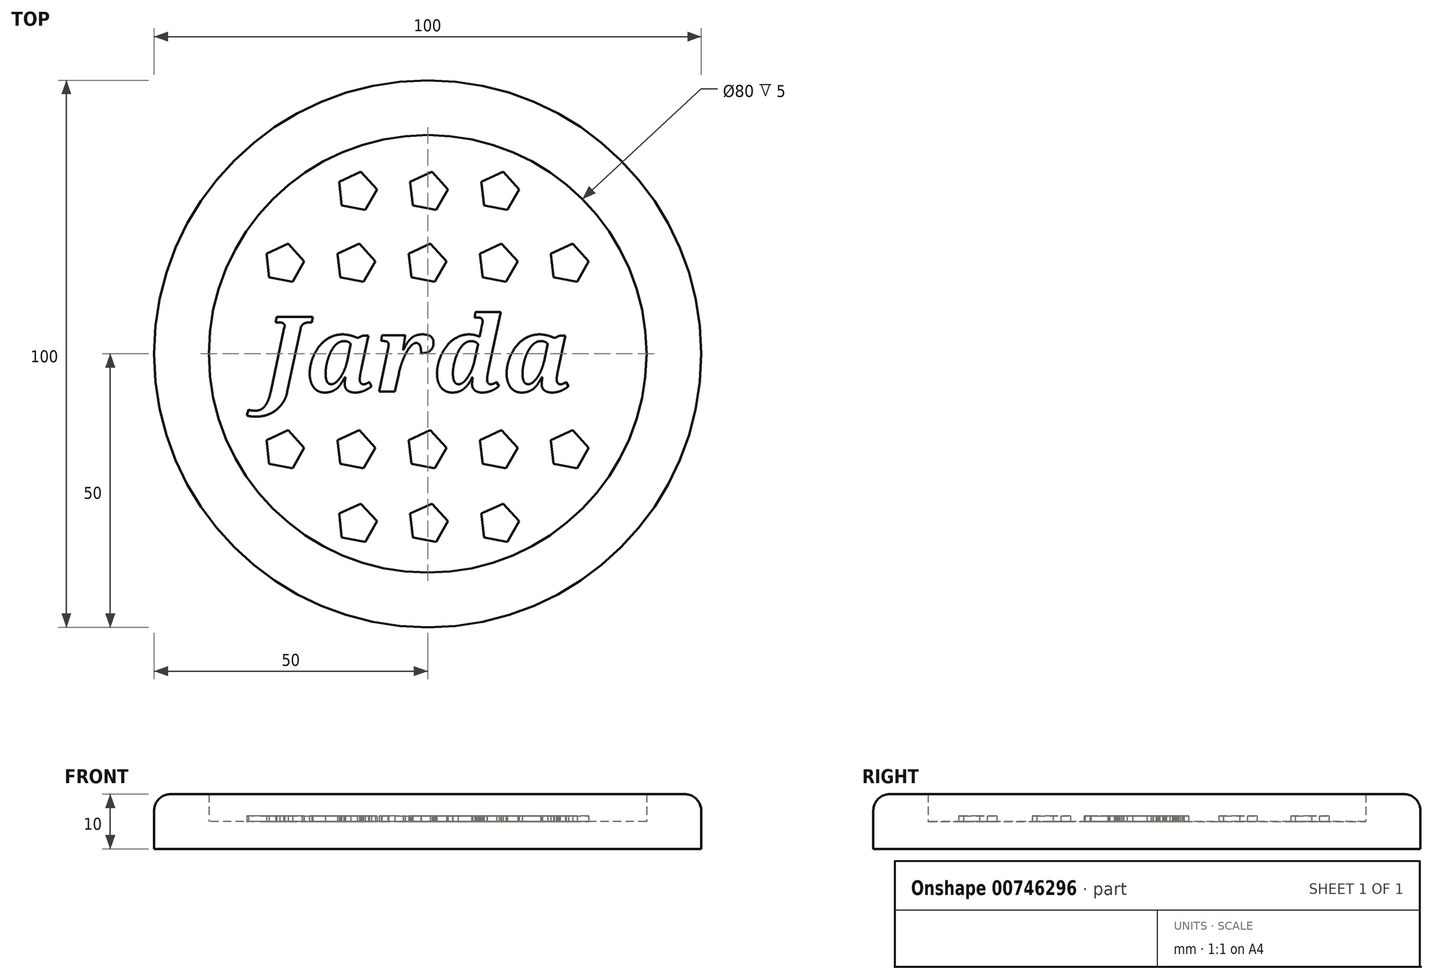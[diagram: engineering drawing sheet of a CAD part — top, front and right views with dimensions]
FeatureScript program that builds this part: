
annotation { "Feature Type Name" : "Feature", "Feature Type Description" : "" }
export const myFeature = defineFeature(function(context is Context, id is Id, definition is map)
    precondition{}
    {
        {
            var Q0;
            Q0=qCreatedBy(makeId("Top.planeOp"),FACE);
            var sketch = newSketch(context, id + "F0", { "sketchPlane" : qUnion([Q0])});
            skCircle(sketch, "E0", {"center": v(0, 0) * mm, "radius": 50 * mm});
            skCircle(sketch, "E1", {"center": v(0, 0) * mm, "radius": 40 * mm});
            skText(sketch, "E2", { "text": "Jarda", "fontName": "NotoSerif-BoldItalic.ttf"});
            skCircle(sketch, "E3.cCircle", {"center": v(-26.24, 16.51) * mm, "radius": 3 * mm, "construction": true});
            skLineSegment(sketch, "E3.0", {"start": v(-22.55, 16.94) * mm, "end": v(-24.7, 13.14) * mm});
            skLineSegment(sketch, "E3.1", {"start": v(-24.7, 13.14) * mm, "end": v(-28.97, 14) * mm});
            skLineSegment(sketch, "E3.2", {"start": v(-28.97, 14) * mm, "end": v(-29.47, 18.34) * mm});
            skLineSegment(sketch, "E3.3", {"start": v(-29.47, 18.34) * mm, "end": v(-25.5, 20.15) * mm});
            skLineSegment(sketch, "E3.4", {"start": v(-25.5, 20.15) * mm, "end": v(-22.55, 16.94) * mm});
            skPoint(sketch, "E3.0.midPoint", {"position": v(-23.62, 15.04) * mm});
            skPoint(sketch, "E4.0.1.0", {"position": v(-23.62, -19.06) * mm});
            skLineSegment(sketch, "E4.0.1.1", {"start": v(-25.5, -13.95) * mm, "end": v(-22.55, -17.16) * mm});
            skLineSegment(sketch, "E4.0.1.2", {"start": v(-29.47, -15.76) * mm, "end": v(-25.5, -13.95) * mm});
            skLineSegment(sketch, "E4.0.1.3", {"start": v(-28.97, -20.1) * mm, "end": v(-29.47, -15.76) * mm});
            skLineSegment(sketch, "E4.0.1.4", {"start": v(-24.7, -20.96) * mm, "end": v(-28.97, -20.1) * mm});
            skCircle(sketch, "E4.0.1.5", {"center": v(-26.24, -17.59) * mm, "radius": 3 * mm, "construction": true});
            skLineSegment(sketch, "E4.0.1.6", {"start": v(-22.55, -17.16) * mm, "end": v(-24.7, -20.96) * mm});
            skPoint(sketch, "E4.1.0.0", {"position": v(-10.62, 15.04) * mm});
            skLineSegment(sketch, "E4.1.0.1", {"start": v(-12.5, 20.15) * mm, "end": v(-9.55, 16.94) * mm});
            skLineSegment(sketch, "E4.1.0.2", {"start": v(-16.47, 18.34) * mm, "end": v(-12.5, 20.15) * mm});
            skLineSegment(sketch, "E4.1.0.3", {"start": v(-15.97, 14) * mm, "end": v(-16.47, 18.34) * mm});
            skLineSegment(sketch, "E4.1.0.4", {"start": v(-11.7, 13.14) * mm, "end": v(-15.97, 14) * mm});
            skCircle(sketch, "E4.1.0.5", {"center": v(-13.24, 16.51) * mm, "radius": 3 * mm, "construction": true});
            skLineSegment(sketch, "E4.1.0.6", {"start": v(-9.55, 16.94) * mm, "end": v(-11.7, 13.14) * mm});
            skPoint(sketch, "E4.1.1.0", {"position": v(-10.62, -19.06) * mm});
            skLineSegment(sketch, "E4.1.1.1", {"start": v(-12.5, -13.95) * mm, "end": v(-9.55, -17.16) * mm});
            skLineSegment(sketch, "E4.1.1.2", {"start": v(-16.47, -15.76) * mm, "end": v(-12.5, -13.95) * mm});
            skLineSegment(sketch, "E4.1.1.3", {"start": v(-15.97, -20.1) * mm, "end": v(-16.47, -15.76) * mm});
            skLineSegment(sketch, "E4.1.1.4", {"start": v(-11.7, -20.96) * mm, "end": v(-15.97, -20.1) * mm});
            skCircle(sketch, "E4.1.1.5", {"center": v(-13.24, -17.59) * mm, "radius": 3 * mm, "construction": true});
            skLineSegment(sketch, "E4.1.1.6", {"start": v(-9.55, -17.16) * mm, "end": v(-11.7, -20.96) * mm});
            skPoint(sketch, "E4.2.0.0", {"position": v(2.38, 15.04) * mm});
            skLineSegment(sketch, "E4.2.0.1", {"start": v(0.5, 20.15) * mm, "end": v(3.45, 16.94) * mm});
            skLineSegment(sketch, "E4.2.0.2", {"start": v(-3.47, 18.34) * mm, "end": v(0.5, 20.15) * mm});
            skLineSegment(sketch, "E4.2.0.3", {"start": v(-2.97, 14) * mm, "end": v(-3.47, 18.34) * mm});
            skLineSegment(sketch, "E4.2.0.4", {"start": v(1.3, 13.14) * mm, "end": v(-2.97, 14) * mm});
            skCircle(sketch, "E4.2.0.5", {"center": v(-0.24, 16.51) * mm, "radius": 3 * mm, "construction": true});
            skLineSegment(sketch, "E4.2.0.6", {"start": v(3.45, 16.94) * mm, "end": v(1.3, 13.14) * mm});
            skPoint(sketch, "E4.2.1.0", {"position": v(2.38, -19.06) * mm});
            skLineSegment(sketch, "E4.2.1.1", {"start": v(0.5, -13.95) * mm, "end": v(3.45, -17.16) * mm});
            skLineSegment(sketch, "E4.2.1.2", {"start": v(-3.47, -15.76) * mm, "end": v(0.5, -13.95) * mm});
            skLineSegment(sketch, "E4.2.1.3", {"start": v(-2.97, -20.1) * mm, "end": v(-3.47, -15.76) * mm});
            skLineSegment(sketch, "E4.2.1.4", {"start": v(1.3, -20.96) * mm, "end": v(-2.97, -20.1) * mm});
            skCircle(sketch, "E4.2.1.5", {"center": v(-0.24, -17.59) * mm, "radius": 3 * mm, "construction": true});
            skLineSegment(sketch, "E4.2.1.6", {"start": v(3.45, -17.16) * mm, "end": v(1.3, -20.96) * mm});
            skPoint(sketch, "E4.3.0.0", {"position": v(15.38, 15.04) * mm});
            skLineSegment(sketch, "E4.3.0.1", {"start": v(13.5, 20.15) * mm, "end": v(16.45, 16.94) * mm});
            skLineSegment(sketch, "E4.3.0.2", {"start": v(9.53, 18.34) * mm, "end": v(13.5, 20.15) * mm});
            skLineSegment(sketch, "E4.3.0.3", {"start": v(10.03, 14) * mm, "end": v(9.53, 18.34) * mm});
            skLineSegment(sketch, "E4.3.0.4", {"start": v(14.3, 13.14) * mm, "end": v(10.03, 14) * mm});
            skCircle(sketch, "E4.3.0.5", {"center": v(12.76, 16.51) * mm, "radius": 3 * mm, "construction": true});
            skLineSegment(sketch, "E4.3.0.6", {"start": v(16.45, 16.94) * mm, "end": v(14.3, 13.14) * mm});
            skPoint(sketch, "E4.3.1.0", {"position": v(15.38, -19.06) * mm});
            skLineSegment(sketch, "E4.3.1.1", {"start": v(13.5, -13.95) * mm, "end": v(16.45, -17.16) * mm});
            skLineSegment(sketch, "E4.3.1.2", {"start": v(9.53, -15.76) * mm, "end": v(13.5, -13.95) * mm});
            skLineSegment(sketch, "E4.3.1.3", {"start": v(10.03, -20.1) * mm, "end": v(9.53, -15.76) * mm});
            skLineSegment(sketch, "E4.3.1.4", {"start": v(14.3, -20.96) * mm, "end": v(10.03, -20.1) * mm});
            skCircle(sketch, "E4.3.1.5", {"center": v(12.76, -17.59) * mm, "radius": 3 * mm, "construction": true});
            skLineSegment(sketch, "E4.3.1.6", {"start": v(16.45, -17.16) * mm, "end": v(14.3, -20.96) * mm});
            skPoint(sketch, "E4.4.0.0", {"position": v(28.38, 15.04) * mm});
            skLineSegment(sketch, "E4.4.0.1", {"start": v(26.5, 20.15) * mm, "end": v(29.45, 16.94) * mm});
            skLineSegment(sketch, "E4.4.0.2", {"start": v(22.53, 18.34) * mm, "end": v(26.5, 20.15) * mm});
            skLineSegment(sketch, "E4.4.0.3", {"start": v(23.03, 14) * mm, "end": v(22.53, 18.34) * mm});
            skLineSegment(sketch, "E4.4.0.4", {"start": v(27.3, 13.14) * mm, "end": v(23.03, 14) * mm});
            skCircle(sketch, "E4.4.0.5", {"center": v(25.76, 16.51) * mm, "radius": 3 * mm, "construction": true});
            skLineSegment(sketch, "E4.4.0.6", {"start": v(29.45, 16.94) * mm, "end": v(27.3, 13.14) * mm});
            skPoint(sketch, "E4.4.1.0", {"position": v(28.38, -19.06) * mm});
            skLineSegment(sketch, "E4.4.1.1", {"start": v(26.5, -13.95) * mm, "end": v(29.45, -17.16) * mm});
            skLineSegment(sketch, "E4.4.1.2", {"start": v(22.53, -15.76) * mm, "end": v(26.5, -13.95) * mm});
            skLineSegment(sketch, "E4.4.1.3", {"start": v(23.03, -20.1) * mm, "end": v(22.53, -15.76) * mm});
            skLineSegment(sketch, "E4.4.1.4", {"start": v(27.3, -20.96) * mm, "end": v(23.03, -20.1) * mm});
            skCircle(sketch, "E4.4.1.5", {"center": v(25.76, -17.59) * mm, "radius": 3 * mm, "construction": true});
            skLineSegment(sketch, "E4.4.1.6", {"start": v(29.45, -17.16) * mm, "end": v(27.3, -20.96) * mm});
            skLineSegment(sketch, "E4.direction1", {"start": v(-28.97, 14) * mm, "end": v(-15.97, 14) * mm, "construction": true});
            skLineSegment(sketch, "E4.direction2", {"start": v(-28.97, 14) * mm, "end": v(-28.97, -20.1) * mm, "construction": true});
            skPoint(sketch, "E5.2.1.0", {"position": v(-10.35, -32.51) * mm});
            skLineSegment(sketch, "E5.2.1.1", {"start": v(-12.23, -27.4) * mm, "end": v(-9.28, -30.61) * mm});
            skLineSegment(sketch, "E5.2.1.2", {"start": v(-16.2, -29.21) * mm, "end": v(-12.23, -27.4) * mm});
            skLineSegment(sketch, "E5.2.1.3", {"start": v(-15.7, -33.54) * mm, "end": v(-16.2, -29.21) * mm});
            skLineSegment(sketch, "E5.2.1.4", {"start": v(-11.42, -34.4) * mm, "end": v(-15.7, -33.54) * mm});
            skCircle(sketch, "E5.2.1.5", {"center": v(-12.96, -31.04) * mm, "radius": 3 * mm, "construction": true});
            skLineSegment(sketch, "E5.2.1.6", {"start": v(-9.28, -30.61) * mm, "end": v(-11.42, -34.4) * mm});
            skLineSegment(sketch, "E6.1.0.0", {"start": v(1.58, -34.4) * mm, "end": v(-2.7, -33.54) * mm});
            skLineSegment(sketch, "E6.1.0.1", {"start": v(-3.2, -29.21) * mm, "end": v(0.77, -27.4) * mm});
            skLineSegment(sketch, "E6.1.0.2", {"start": v(0.77, -27.4) * mm, "end": v(3.72, -30.61) * mm});
            skPoint(sketch, "E6.1.0.3", {"position": v(2.65, -32.51) * mm});
            skLineSegment(sketch, "E6.1.0.4", {"start": v(-2.7, -33.54) * mm, "end": v(-3.2, -29.21) * mm});
            skLineSegment(sketch, "E6.1.0.5", {"start": v(3.72, -30.61) * mm, "end": v(1.58, -34.4) * mm});
            skCircle(sketch, "E6.1.0.6", {"center": v(0.04, -31.04) * mm, "radius": 3 * mm, "construction": true});
            skLineSegment(sketch, "E6.2.0.0", {"start": v(14.58, -34.4) * mm, "end": v(10.3, -33.54) * mm});
            skLineSegment(sketch, "E6.2.0.1", {"start": v(9.8, -29.21) * mm, "end": v(13.77, -27.4) * mm});
            skLineSegment(sketch, "E6.2.0.2", {"start": v(13.77, -27.4) * mm, "end": v(16.72, -30.61) * mm});
            skPoint(sketch, "E6.2.0.3", {"position": v(15.65, -32.51) * mm});
            skLineSegment(sketch, "E6.2.0.4", {"start": v(10.3, -33.54) * mm, "end": v(9.8, -29.21) * mm});
            skLineSegment(sketch, "E6.2.0.5", {"start": v(16.72, -30.61) * mm, "end": v(14.58, -34.4) * mm});
            skCircle(sketch, "E6.2.0.6", {"center": v(13.04, -31.04) * mm, "radius": 3 * mm, "construction": true});
            skLineSegment(sketch, "E6.direction1", {"start": v(-15.7, -33.54) * mm, "end": v(-2.7, -33.54) * mm, "construction": true});
            skLineSegment(sketch, "E7.0.1.0", {"start": v(1.58, 26.3) * mm, "end": v(-2.7, 27.16) * mm});
            skLineSegment(sketch, "E7.0.1.1", {"start": v(0.77, 33.3) * mm, "end": v(3.72, 30.09) * mm});
            skLineSegment(sketch, "E7.0.1.2", {"start": v(-15.7, 27.16) * mm, "end": v(-2.7, 27.16) * mm, "construction": true});
            skLineSegment(sketch, "E7.0.1.3", {"start": v(-12.23, 33.3) * mm, "end": v(-9.28, 30.09) * mm});
            skPoint(sketch, "E7.0.1.4", {"position": v(-10.35, 28.19) * mm});
            skLineSegment(sketch, "E7.0.1.5", {"start": v(-2.7, 27.16) * mm, "end": v(-3.2, 31.49) * mm});
            skCircle(sketch, "E7.0.1.6", {"center": v(-12.96, 29.66) * mm, "radius": 3 * mm, "construction": true});
            skPoint(sketch, "E7.0.1.7", {"position": v(2.65, 28.19) * mm});
            skCircle(sketch, "E7.0.1.8", {"center": v(0.04, 29.66) * mm, "radius": 3 * mm, "construction": true});
            skLineSegment(sketch, "E7.0.1.9", {"start": v(14.58, 26.3) * mm, "end": v(10.3, 27.16) * mm});
            skPoint(sketch, "E7.0.1.10", {"position": v(15.65, 28.19) * mm});
            skCircle(sketch, "E7.0.1.11", {"center": v(13.04, 29.66) * mm, "radius": 3 * mm, "construction": true});
            skLineSegment(sketch, "E7.0.1.12", {"start": v(-9.28, 30.09) * mm, "end": v(-11.42, 26.3) * mm});
            skLineSegment(sketch, "E7.0.1.13", {"start": v(-3.2, 31.49) * mm, "end": v(0.77, 33.3) * mm});
            skLineSegment(sketch, "E7.0.1.14", {"start": v(-15.7, 27.16) * mm, "end": v(-16.2, 31.49) * mm});
            skLineSegment(sketch, "E7.0.1.15", {"start": v(-11.42, 26.3) * mm, "end": v(-15.7, 27.16) * mm});
            skLineSegment(sketch, "E7.0.1.16", {"start": v(3.72, 30.09) * mm, "end": v(1.58, 26.3) * mm});
            skLineSegment(sketch, "E7.0.1.17", {"start": v(16.72, 30.09) * mm, "end": v(14.58, 26.3) * mm});
            skLineSegment(sketch, "E7.0.1.18", {"start": v(9.8, 31.49) * mm, "end": v(13.77, 33.3) * mm});
            skLineSegment(sketch, "E7.0.1.19", {"start": v(13.77, 33.3) * mm, "end": v(16.72, 30.09) * mm});
            skLineSegment(sketch, "E7.0.1.20", {"start": v(10.3, 27.16) * mm, "end": v(9.8, 31.49) * mm});
            skLineSegment(sketch, "E7.0.1.21", {"start": v(-16.2, 31.49) * mm, "end": v(-12.23, 33.3) * mm});
            skLineSegment(sketch, "E7.direction1", {"start": v(-15.7, -33.54) * mm, "end": v(9.3, -33.54) * mm, "construction": true});
            skLineSegment(sketch, "E7.direction2", {"start": v(-15.7, -33.54) * mm, "end": v(-15.7, 27.16) * mm, "construction": true});
            const initialGuessF0  = {"E2": [-0.03, -0.00689, 1, 0, 0.01378]};
            skSetInitialGuess(sketch, initialGuessF0);
            skSolve(sketch);
        }
        {
            var Q0;
            Q0=makeQuery(id+"F0.imprint","IMPRINT",FACE,{"disambiguationData":[TD([[makeQuery(id+"F0.imprint","IMPRINT",EDGE,{"derivedFrom":sQuery(id+"F0.wireOp",EDGE,"E0")}),1.0]])]});
            extrude(context, id + "F1", {"entities" : qUnion([Q0]), "depth" : 10 * mm, "offsetDistance" : 25 * mm});
        }
        {
            var Q0;
            Q0=makeQuery(id+"F0.imprint","IMPRINT",FACE,{"disambiguationData":[TD([[makeQuery(id+"F0.imprint","IMPRINT",EDGE,{"derivedFrom":sQuery(id+"F0.wireOp",EDGE,"E3.0")}),-1.0]])]});
            var Q1;
            Q1=makeQuery(id+"F0.imprint","IMPRINT",FACE,{"disambiguationData":[TD([[makeQuery(id+"F0.imprint","IMPRINT",EDGE,{"derivedFrom":sQuery(id+"F0.wireOp",EDGE,"E4.1.0.1")}),-1.0]])]});
            var Q2;
            Q2=makeQuery(id+"F0.imprint","IMPRINT",FACE,{"disambiguationData":[TD([[makeQuery(id+"F0.imprint","IMPRINT",EDGE,{"derivedFrom":sQuery(id+"F0.wireOp",EDGE,"E7.0.1.3")}),-1.0]])]});
            var Q3;
            Q3=makeQuery(id+"F0.imprint","IMPRINT",FACE,{"disambiguationData":[TD([[makeQuery(id+"F0.imprint","IMPRINT",EDGE,{"derivedFrom":sQuery(id+"F0.wireOp",EDGE,"E7.0.1.0")}),-1.0]])]});
            var Q4;
            Q4=makeQuery(id+"F0.imprint","IMPRINT",FACE,{"disambiguationData":[TD([[makeQuery(id+"F0.imprint","IMPRINT",EDGE,{"derivedFrom":sQuery(id+"F0.wireOp",EDGE,"E4.2.0.1")}),-1.0]])]});
            var Q5;
            Q5=makeQuery(id+"F0.imprint","IMPRINT",FACE,{"disambiguationData":[TD([[makeQuery(id+"F0.imprint","IMPRINT",EDGE,{"derivedFrom":sQuery(id+"F0.wireOp",EDGE,"E7.0.1.9")}),-1.0]])]});
            var Q6;
            Q6=makeQuery(id+"F0.imprint","IMPRINT",FACE,{"disambiguationData":[TD([[makeQuery(id+"F0.imprint","IMPRINT",EDGE,{"derivedFrom":sQuery(id+"F0.wireOp",EDGE,"E4.3.0.1")}),-1.0]])]});
            var Q7;
            Q7=makeQuery(id+"F0.imprint","IMPRINT",FACE,{"disambiguationData":[TD([[makeQuery(id+"F0.imprint","IMPRINT",EDGE,{"derivedFrom":sQuery(id+"F0.wireOp",EDGE,"E4.4.0.1")}),-1.0]])]});
            var Q8;
            Q8=makeQuery(id+"F0.imprint","IMPRINT",FACE,{"disambiguationData":[TD([[makeQuery(id+"F0.imprint","IMPRINT",EDGE,{"derivedFrom":sQuery(id+"F0.wireOp",EDGE,"E2.sketch_text.stroke-0")}),-1.0]])]});
            var Q9;
            Q9=makeQuery(id+"F0.imprint","IMPRINT",FACE,{"disambiguationData":[TD([[makeQuery(id+"F0.imprint","IMPRINT",EDGE,{"derivedFrom":sQuery(id+"F0.wireOp",EDGE,"E2.sketch_text.stroke-32")}),-1.0]])]});
            var Q10;
            Q10=makeQuery(id+"F0.imprint","IMPRINT",FACE,{"disambiguationData":[TD([[makeQuery(id+"F0.imprint","IMPRINT",EDGE,{"derivedFrom":sQuery(id+"F0.wireOp",EDGE,"E2.sketch_text.stroke-88")}),-1.0]])]});
            var Q11;
            Q11=makeQuery(id+"F0.imprint","IMPRINT",FACE,{"disambiguationData":[TD([[makeQuery(id+"F0.imprint","IMPRINT",EDGE,{"derivedFrom":sQuery(id+"F0.wireOp",EDGE,"E2.sketch_text.stroke-118")}),-1.0]])]});
            var Q12;
            Q12=makeQuery(id+"F0.imprint","IMPRINT",FACE,{"disambiguationData":[TD([[makeQuery(id+"F0.imprint","IMPRINT",EDGE,{"derivedFrom":sQuery(id+"F0.wireOp",EDGE,"E2.sketch_text.stroke-190")}),-1.0]])]});
            var Q13;
            Q13=makeQuery(id+"F0.imprint","IMPRINT",FACE,{"disambiguationData":[TD([[makeQuery(id+"F0.imprint","IMPRINT",EDGE,{"derivedFrom":sQuery(id+"F0.wireOp",EDGE,"E4.0.1.1")}),-1.0]])]});
            var Q14;
            Q14=makeQuery(id+"F0.imprint","IMPRINT",FACE,{"disambiguationData":[TD([[makeQuery(id+"F0.imprint","IMPRINT",EDGE,{"derivedFrom":sQuery(id+"F0.wireOp",EDGE,"E4.1.1.1")}),-1.0]])]});
            var Q15;
            Q15=makeQuery(id+"F0.imprint","IMPRINT",FACE,{"disambiguationData":[TD([[makeQuery(id+"F0.imprint","IMPRINT",EDGE,{"derivedFrom":sQuery(id+"F0.wireOp",EDGE,"E4.2.1.1")}),-1.0]])]});
            var Q16;
            Q16=makeQuery(id+"F0.imprint","IMPRINT",FACE,{"disambiguationData":[TD([[makeQuery(id+"F0.imprint","IMPRINT",EDGE,{"derivedFrom":sQuery(id+"F0.wireOp",EDGE,"E4.3.1.1")}),-1.0]])]});
            var Q17;
            Q17=makeQuery(id+"F0.imprint","IMPRINT",FACE,{"disambiguationData":[TD([[makeQuery(id+"F0.imprint","IMPRINT",EDGE,{"derivedFrom":sQuery(id+"F0.wireOp",EDGE,"E4.4.1.1")}),-1.0]])]});
            var Q18;
            Q18=makeQuery(id+"F0.imprint","IMPRINT",FACE,{"disambiguationData":[TD([[makeQuery(id+"F0.imprint","IMPRINT",EDGE,{"derivedFrom":sQuery(id+"F0.wireOp",EDGE,"E6.2.0.0")}),-1.0]])]});
            var Q19;
            Q19=makeQuery(id+"F0.imprint","IMPRINT",FACE,{"disambiguationData":[TD([[makeQuery(id+"F0.imprint","IMPRINT",EDGE,{"derivedFrom":sQuery(id+"F0.wireOp",EDGE,"E6.1.0.0")}),-1.0]])]});
            var Q20;
            Q20=makeQuery(id+"F0.imprint","IMPRINT",FACE,{"disambiguationData":[TD([[makeQuery(id+"F0.imprint","IMPRINT",EDGE,{"derivedFrom":sQuery(id+"F0.wireOp",EDGE,"E5.2.1.1")}),-1.0]])]});
            extrude(context, id + "F2", {"entities" : qUnion([Q0, Q1, Q2, Q3, Q4, Q5, Q6, Q7, Q8, Q9, Q10, Q11, Q12, Q13, Q14, Q15, Q16, Q17, Q18, Q19, Q20]), "operationType" : NewBodyOperationType.ADD, "depth" : 6 * mm, "offsetDistance" : 25 * mm});
        }
        {
            var Q0;
            Q0=makeQuery(id+"F0.imprint","IMPRINT",FACE,{"disambiguationData":[TD([[makeQuery(id+"F0.imprint","IMPRINT",EDGE,{"derivedFrom":sQuery(id+"F0.wireOp",EDGE,"E1")}),1.0]])]});
            var Q1;
            Q1=makeQuery(id+"F0.imprint","IMPRINT",FACE,{"disambiguationData":[TD([[makeQuery(id+"F0.imprint","IMPRINT",EDGE,{"derivedFrom":sQuery(id+"F0.wireOp",EDGE,"E2.sketch_text.stroke-118")}),1.0]])]});
            var Q2;
            Q2=makeQuery(id+"F0.imprint","IMPRINT",FACE,{"disambiguationData":[TD([[makeQuery(id+"F0.imprint","IMPRINT",EDGE,{"derivedFrom":sQuery(id+"F0.wireOp",EDGE,"E2.sketch_text.stroke-229")}),1.0]])]});
            var Q3;
            Q3=makeQuery(id+"F0.imprint","IMPRINT",FACE,{"disambiguationData":[TD([[makeQuery(id+"F0.imprint","IMPRINT",EDGE,{"derivedFrom":sQuery(id+"F0.wireOp",EDGE,"E2.sketch_text.stroke-71")}),1.0]])]});
            extrude(context, id + "F3", {"entities" : qUnion([Q0, Q1, Q2, Q3]), "operationType" : NewBodyOperationType.ADD, "depth" : 5 * mm, "offsetDistance" : 25 * mm});
        }
        {
            var Q0;
            Q0=makeQuery(id+"F1.opExtrude","CAP_EDGE",EDGE,{"disambiguationData":[OSD([sQuery(id+"F0.wireOp",EDGE,"E0")])],"isStart":false});
            fillet(context, id + "F4", {"entities" : qUnion([Q0]), "radius" : 3 * mm, "tangentPropagation" : true, "allowEdgeOverflow" : false});
        }
    });
